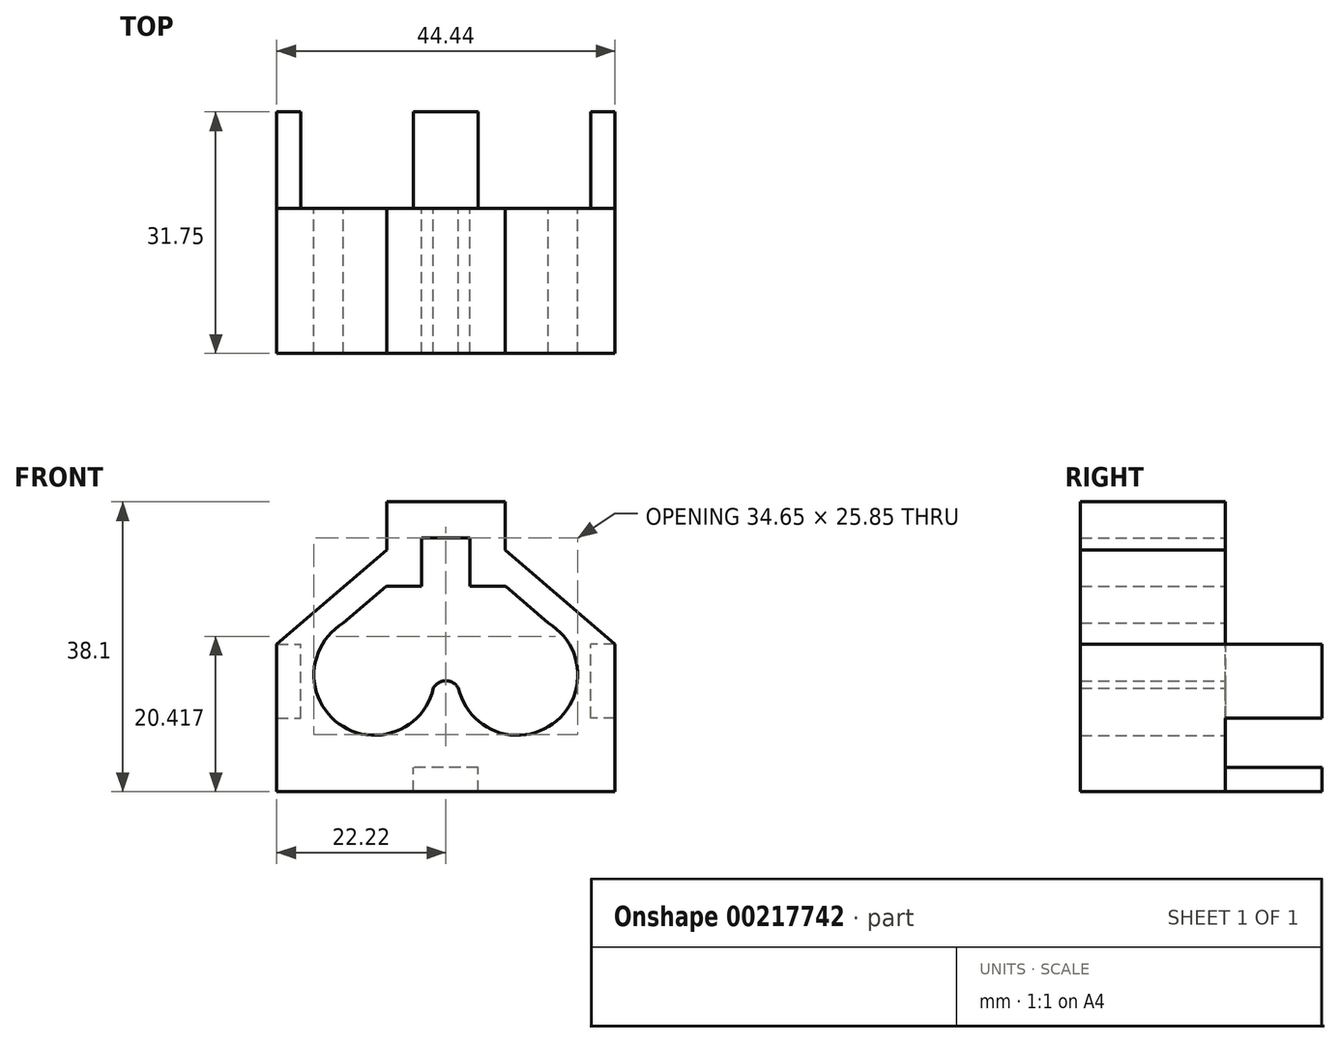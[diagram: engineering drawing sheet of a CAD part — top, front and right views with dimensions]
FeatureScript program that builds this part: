
annotation { "Feature Type Name" : "Feature", "Feature Type Description" : "" }
export const myFeature = defineFeature(function(context is Context, id is Id, definition is map)
    precondition{}
    {
        {
            var Q0;
            Q0=qCreatedBy(makeId("Front.planeOp"),FACE);
            var sketch = newSketch(context, id + "F0", { "sketchPlane" : qUnion([Q0])});
            skLineSegment(sketch, "E0", {"start": v(0, 0.13) * mm, "end": v(7.5, 0.13) * mm});
            skLineSegment(sketch, "E1", {"start": v(-22.22, 19.5) * mm, "end": v(-22.22, 4.52) * mm});
            skLineSegment(sketch, "E2", {"start": v(-7.5, 0.13) * mm, "end": v(0, 0.13) * mm});
            skArc(sketch, "E3", {"start": v(-13.47, 22.3) * mm, "mid": v(-14.04, 9.06) * mm, "end": v(-1.65, 13.77) * mm});
            skArc(sketch, "E4.MirrorC", {"start": v(13.47, 22.3) * mm, "mid": v(14.05, 9.06) * mm, "end": v(1.65, 13.75) * mm});
            skArc(sketch, "E5", {"start": v(1.65, 13.75) * mm, "mid": v(0, 14.71) * mm, "end": v(-1.65, 13.77) * mm});
            skLineSegment(sketch, "E6", {"start": v(-22.22, 19.5) * mm, "end": v(-22.22, 0.13) * mm});
            skLineSegment(sketch, "E7.MirrorCS", {"start": v(22.22, 19.5) * mm, "end": v(22.22, 0.13) * mm});
            skLineSegment(sketch, "E8", {"start": v(0, 0.13) * mm, "end": v(-22.22, 0.13) * mm});
            skLineSegment(sketch, "E9", {"start": v(0, 0.13) * mm, "end": v(22.22, 0.13) * mm});
            skPoint(sketch, "E10.orphan", {"position": v(-22.22, 0) * mm});
            skLineSegment(sketch, "E11", {"start": v(-3.18, 27.12) * mm, "end": v(-3.18, 30.3) * mm});
            skLineSegment(sketch, "E12", {"start": v(3.17, 30.3) * mm, "end": v(3.17, 27.12) * mm});
            skLineSegment(sketch, "E13", {"start": v(3.17, 27.12) * mm, "end": v(3.17, 27.12) * mm});
            skLineSegment(sketch, "E14", {"start": v(-22.22, 19.5) * mm, "end": v(-7.77, 31.88) * mm});
            skLineSegment(sketch, "E15", {"start": v(-3.18, 27.12) * mm, "end": v(-7.84, 27.12) * mm});
            skLineSegment(sketch, "E16", {"start": v(-13.47, 22.3) * mm, "end": v(-7.84, 27.12) * mm});
            skLineSegment(sketch, "E17.MirrorCS", {"start": v(3.17, 27.12) * mm, "end": v(7.84, 27.12) * mm});
            skLineSegment(sketch, "E18.MirrorCS", {"start": v(13.46, 22.3) * mm, "end": v(7.84, 27.12) * mm});
            skLineSegment(sketch, "E19.MirrorCS", {"start": v(3.17, 30.3) * mm, "end": v(3.18, 30.3) * mm});
            skLineSegment(sketch, "E20.MirrorCS", {"start": v(22.22, 19.5) * mm, "end": v(7.77, 31.88) * mm});
            skPoint(sketch, "E21.end.orphan", {"position": v(-9.63, 30.3) * mm});
            skPoint(sketch, "E22.orphan", {"position": v(9.62, 30.3) * mm});
            skPoint(sketch, "E23.start.orphan", {"position": v(0, 27.12) * mm});
            skLineSegment(sketch, "E24", {"start": v(13.47, 22.3) * mm, "end": v(7.84, 27.12) * mm});
            skLineSegment(sketch, "E25", {"start": v(3.17, 27.12) * mm, "end": v(3.17, 30.3) * mm});
            skLineSegment(sketch, "E26", {"start": v(-3.18, 30.3) * mm, "end": v(-3.18, 27.12) * mm});
            skLineSegment(sketch, "E27", {"start": v(-7.84, 27.12) * mm, "end": v(-13.47, 22.3) * mm});
            skArc(sketch, "E28", {"start": v(1.65, 13.75) * mm, "mid": v(14.06, 9.07) * mm, "end": v(13.45, 22.31) * mm});
            skPoint(sketch, "E29.startSnap0", {"position": v(0, 30.3) * mm});
            skPoint(sketch, "E30.orphan", {"position": v(22.22, 2.54) * mm});
            skLineSegment(sketch, "E31", {"start": v(3.17, 30.3) * mm, "end": v(3.17, 33.47) * mm});
            skLineSegment(sketch, "E32", {"start": v(3.17, 33.47) * mm, "end": v(-3.18, 33.47) * mm});
            skLineSegment(sketch, "E33", {"start": v(-3.18, 33.47) * mm, "end": v(-3.18, 30.3) * mm});
            skLineSegment(sketch, "E34", {"start": v(-7.77, 31.88) * mm, "end": v(-7.77, 38.23) * mm});
            skLineSegment(sketch, "E35", {"start": v(7.77, 31.88) * mm, "end": v(7.77, 38.23) * mm});
            skLineSegment(sketch, "E36", {"start": v(7.77, 38.23) * mm, "end": v(-7.77, 38.23) * mm});
            skCircle(sketch, "E37", {"center": v(-9.4, 15.5) * mm, "radius": 7.94 * mm});
            skCircle(sketch, "E38", {"center": v(9.4, 15.5) * mm, "radius": 7.94 * mm});
            skCircle(sketch, "E39", {"center": v(0, 23.08) * mm, "radius": 3.97 * mm});
            skSolve(sketch);
        }
        {
            var Q0;
            Q0 = qSketchRegion(id + "F0", true);
            extrude(context, id + "F1", {"entities" : qUnion([Q0]), "depth" : 19.05 * mm});
        }
        {
            var Q0;
            Q0=makeQuery(id+"F1.opExtrude","CAP_FACE",FACE,{"disambiguationData":[OSD([sQuery(id+"F0.wireOp",EDGE,"E3"),sQuery(id+"F0.wireOp",EDGE,"E4.MirrorC"),sQuery(id+"F0.wireOp",EDGE,"UpXB3lFz-6tCb-G21y-YKDH-iTufkDb4iGxh"),sQuery(id+"F0.wireOp",EDGE,"e5710114-c6b0-443e-928c-83acc31821250.MirrorCS"),sQuery(id+"F0.wireOp",EDGE,"E5"),sQuery(id+"F0.wireOp",EDGE,"E6"),sQuery(id+"F0.wireOp",EDGE,"E7.MirrorCS"),sQuery(id+"F0.wireOp",EDGE,"YnKvE3on-WrPE-iA2C-ydwn-6QHyQp48ySO5"),sQuery(id+"F0.wireOp",EDGE,"E8"),sQuery(id+"F0.wireOp",EDGE,"E9"),sQuery(id+"F0.wireOp",EDGE,"hG3vjqwb-EbUr-b3is-ZpRh-0kJelBgIxYab"),sQuery(id+"F0.wireOp",EDGE,"NGSTyCfK-NuB3-KJgR-2MXq-EnwBM4SVeB3J"),sQuery(id+"F0.wireOp",EDGE,"S73DKJRn-LpNk-oxcx-OfSW-kCXGsYrHIW8I")])],"isStart":true});
            var sketch = newSketch(context, id + "F2", { "sketchPlane" : qUnion([Q0])});
            skLineSegment(sketch, "E40.bottom", {"start": v(-22.22, 19.5) * mm, "end": v(-19.04, 19.5) * mm});
            skLineSegment(sketch, "E40.top", {"start": v(-22.22, 19.5) * mm, "end": v(-19.04, 19.5) * mm});
            skLineSegment(sketch, "E40.left", {"start": v(-22.22, 19.5) * mm, "end": v(-22.22, 19.5) * mm});
            skLineSegment(sketch, "E40.right", {"start": v(-19.04, 19.5) * mm, "end": v(-19.04, 19.5) * mm});
            skLineSegment(sketch, "E41.bottom", {"start": v(22.22, 19.5) * mm, "end": v(19.05, 19.5) * mm});
            skLineSegment(sketch, "E41.top", {"start": v(22.22, 19.5) * mm, "end": v(19.05, 19.5) * mm});
            skLineSegment(sketch, "E41.left", {"start": v(22.22, 19.5) * mm, "end": v(22.22, 19.5) * mm});
            skLineSegment(sketch, "E41.right", {"start": v(19.05, 19.5) * mm, "end": v(19.05, 19.5) * mm});
            skLineSegment(sketch, "E42.bottom", {"start": v(-4.24, 0.13) * mm, "end": v(4.24, 0.13) * mm});
            skLineSegment(sketch, "E42.top", {"start": v(-4.24, 3.3) * mm, "end": v(4.24, 3.3) * mm});
            skLineSegment(sketch, "E43.bottom", {"start": v(22.22, 9.82) * mm, "end": v(19.05, 9.82) * mm});
            skLineSegment(sketch, "E43.left", {"start": v(22.22, 9.82) * mm, "end": v(22.22, 19.5) * mm});
            skLineSegment(sketch, "E43.right", {"start": v(19.05, 9.82) * mm, "end": v(19.05, 19.5) * mm});
            skLineSegment(sketch, "E44.bottom", {"start": v(-22.22, 9.82) * mm, "end": v(-19.04, 9.82) * mm});
            skLineSegment(sketch, "E44.left", {"start": v(-22.22, 9.82) * mm, "end": v(-22.22, 19.5) * mm});
            skLineSegment(sketch, "E44.right", {"start": v(-19.04, 9.82) * mm, "end": v(-19.04, 19.5) * mm});
            skLineSegment(sketch, "E45", {"start": v(0, 0.13) * mm, "end": v(4.24, 0.13) * mm});
            skLineSegment(sketch, "E46", {"start": v(4.24, 0.13) * mm, "end": v(4.24, 3.3) * mm});
            skLineSegment(sketch, "E47", {"start": v(0, 0.13) * mm, "end": v(-4.24, 0.13) * mm});
            skLineSegment(sketch, "E48", {"start": v(-4.24, 0.13) * mm, "end": v(-4.24, 3.3) * mm});
            skPoint(sketch, "E42.right.end.orphan", {"position": v(22.22, 3.3) * mm});
            skPoint(sketch, "E49.orphan", {"position": v(22.22, 0.13) * mm});
            skPoint(sketch, "E42.left.start.orphan", {"position": v(-22.22, 0.13) * mm});
            skSolve(sketch);
        }
        {
            var Q0;
            Q0 = qSketchRegion(id + "F2", true);
            extrude(context, id + "F3", {"entities" : qUnion([Q0]), "operationType" : NewBodyOperationType.ADD, "depth" : 12.7 * mm});
        }
    });
